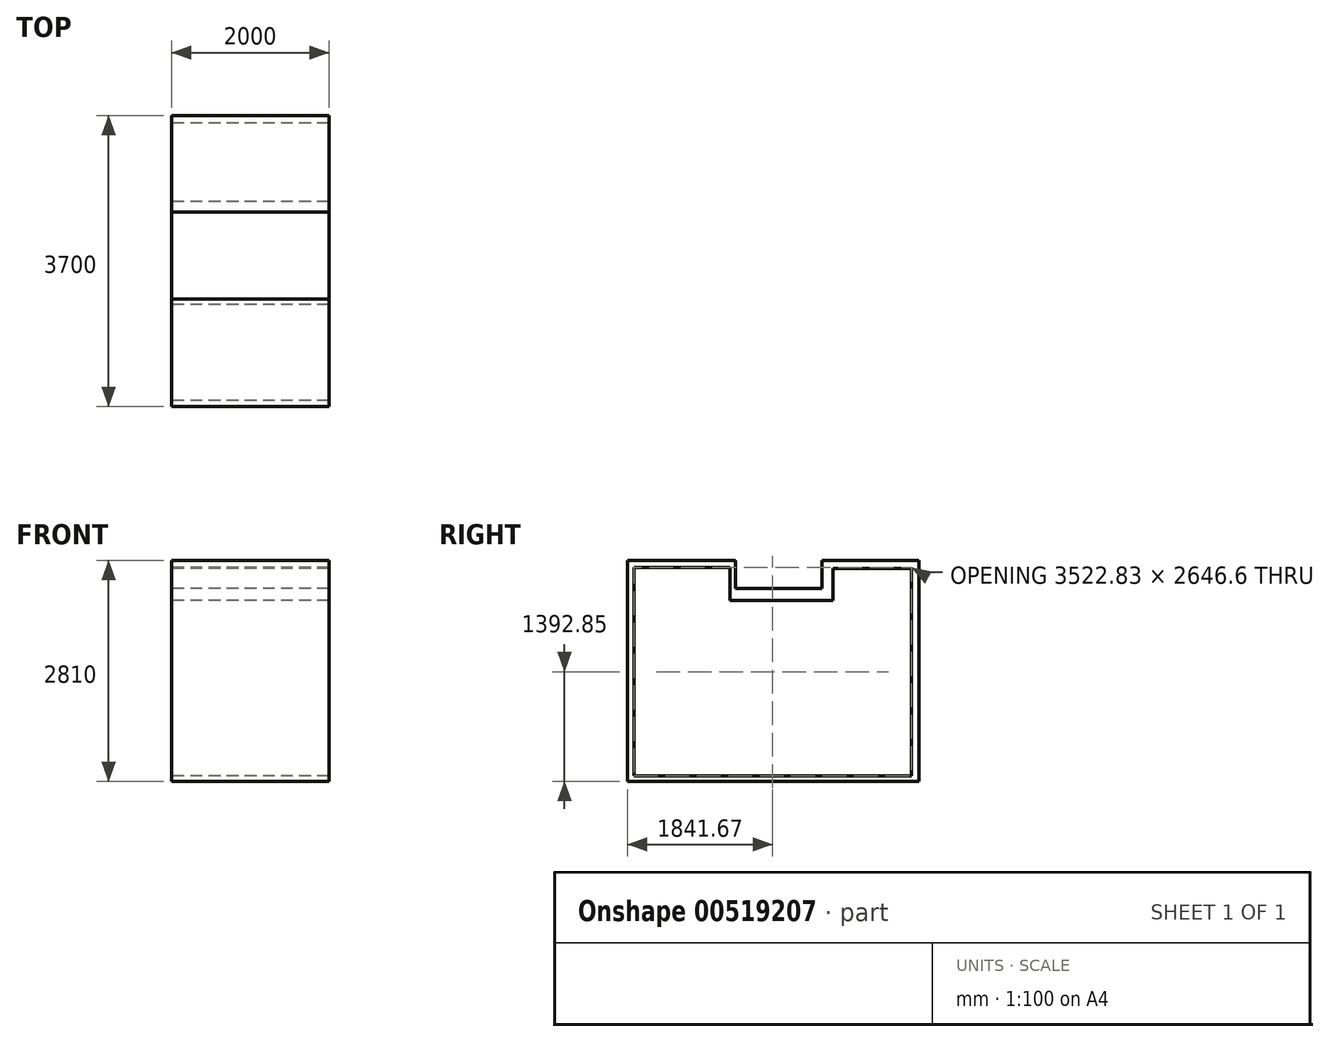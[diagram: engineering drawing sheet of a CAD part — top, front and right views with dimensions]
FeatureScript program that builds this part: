
annotation { "Feature Type Name" : "Feature", "Feature Type Description" : "" }
export const myFeature = defineFeature(function(context is Context, id is Id, definition is map)
    precondition{}
    {
        {
            var Q0;
            Q0=qCreatedBy(makeId("Right.planeOp"),FACE);
            var sketch = newSketch(context, id + "F0", { "sketchPlane" : qUnion([Q0])});
            skLineSegment(sketch, "E0.bottom", {"start": v(-1850, 1405) * mm, "end": v(-480, 1405) * mm});
            skLineSegment(sketch, "E0.top", {"start": v(-1850, -1405) * mm, "end": v(1850, -1405) * mm});
            skLineSegment(sketch, "E0.left", {"start": v(-1850, 1405) * mm, "end": v(-1850, -1405) * mm});
            skLineSegment(sketch, "E0.right", {"start": v(1850, 1405) * mm, "end": v(1850, -1405) * mm});
            skPoint(sketch, "E0.middle", {"position": v(0, 0) * mm});
            skLineSegment(sketch, "E1", {"start": v(620, 1405) * mm, "end": v(620, 1045) * mm});
            skLineSegment(sketch, "E2", {"start": v(620, 1045) * mm, "end": v(-480, 1045) * mm});
            skLineSegment(sketch, "E3", {"start": v(-480, 1045) * mm, "end": v(-480, 1405) * mm});
            skLineSegment(sketch, "E4.trimOffspring", {"start": v(620, 1405) * mm, "end": v(1850, 1405) * mm});
            skLineSegment(sketch, "E5", {"start": v(-1769.74, 1311.15) * mm, "end": v(-1769.74, -1335.45) * mm});
            skLineSegment(sketch, "E6", {"start": v(-1769.74, -1335.45) * mm, "end": v(1753.1, -1335.45) * mm});
            skLineSegment(sketch, "E7", {"start": v(1753.1, -1335.45) * mm, "end": v(1753.1, 1303.41) * mm});
            skLineSegment(sketch, "E8", {"start": v(1753.1, 1303.41) * mm, "end": v(756.18, 1303.41) * mm});
            skLineSegment(sketch, "E9", {"start": v(756.18, 1303.41) * mm, "end": v(756.18, 895.38) * mm});
            skLineSegment(sketch, "E10", {"start": v(756.18, 895.38) * mm, "end": v(-549.24, 895.38) * mm});
            skLineSegment(sketch, "E11", {"start": v(-549.24, 895.38) * mm, "end": v(-549.24, 1311.15) * mm});
            skLineSegment(sketch, "E12", {"start": v(-549.24, 1311.15) * mm, "end": v(-1769.74, 1311.15) * mm});
            skSolve(sketch);
        }
        {
            var Q0;
            Q0 = qSketchRegion(id + "F0", true);
            extrude(context, id + "F1", {"entities" : qUnion([Q0]), "depth" : 2000 * mm, "offsetDistance" : 25 * mm});
        }
    });
